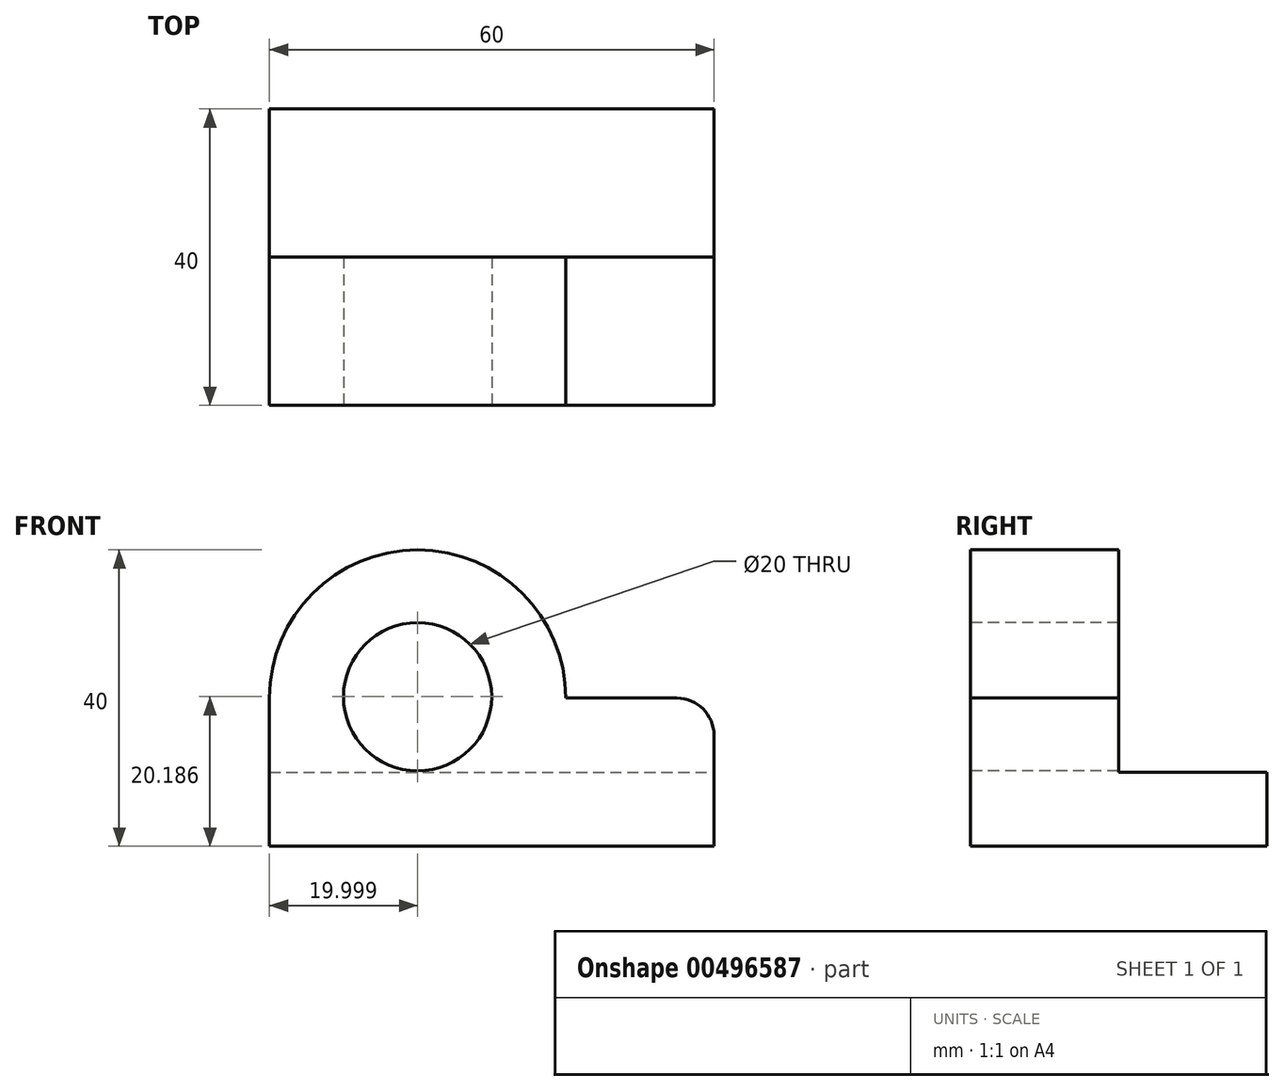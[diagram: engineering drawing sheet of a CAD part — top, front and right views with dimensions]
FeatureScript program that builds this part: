
annotation { "Feature Type Name" : "Feature", "Feature Type Description" : "" }
export const myFeature = defineFeature(function(context is Context, id is Id, definition is map)
    precondition{}
    {
        {
            var Q0;
            Q0=qCreatedBy(makeId("Top.planeOp"),FACE);
            var sketch = newSketch(context, id + "F0", { "sketchPlane" : qUnion([Q0])});
            skLineSegment(sketch, "E0.bottom", {"start": v(0, 0) * mm, "end": v(60, 0) * mm});
            skLineSegment(sketch, "E0.top", {"start": v(0, 40) * mm, "end": v(60, 40) * mm});
            skLineSegment(sketch, "E0.left", {"start": v(0, 0) * mm, "end": v(0, 40) * mm});
            skLineSegment(sketch, "E0.right", {"start": v(60, 0) * mm, "end": v(60, 40) * mm});
            skSolve(sketch);
        }
        {
            var Q0;
            Q0 = qSketchRegion(id + "F0", true);
            extrude(context, id + "F1", {"entities" : qUnion([Q0]), "depth" : 10 * mm});
        }
        {
            var Q0;
            Q0=makeQuery(id+"F1.opExtrude","SWEPT_FACE",FACE,{"disambiguationData":[OSD([sQuery(id+"F0.wireOp",EDGE,"E0.bottom")])]});
            var sketch = newSketch(context, id + "F2", { "sketchPlane" : qUnion([Q0])});
            skPoint(sketch, "E1", {"position": v(20, 20) * mm});
            skArc(sketch, "E2", {"start": v(40, 20) * mm, "mid": v(20, 40) * mm, "end": v(0, 20) * mm});
            skLineSegment(sketch, "E3", {"start": v(0, 20) * mm, "end": v(0, 10) * mm});
            skLineSegment(sketch, "E4", {"start": v(40, 20) * mm, "end": v(55, 20) * mm});
            skLineSegment(sketch, "E5", {"start": v(60, 15) * mm, "end": v(60, 10) * mm});
            skPoint(sketch, "E6.visualSharp", {"position": v(59.99, 20) * mm});
            skArc(sketch, "E6.filletArc", {"start": v(60, 15) * mm, "mid": v(58.53, 18.54) * mm, "end": v(55, 20) * mm});
            skLineSegment(sketch, "E7", {"start": v(0, 10) * mm, "end": v(60, 10) * mm});
            skSolve(sketch);
        }
        {
            var Q0;
            Q0 = qSketchRegion(id + "F2", true);
            extrude(context, id + "F3", {"entities" : qUnion([Q0]), "operationType" : NewBodyOperationType.ADD, "oppositeDirection" : true, "depth" : 20 * mm});
        }
        {
            var Q0;
            Q0=qCreatedBy(makeId("Front.planeOp"),FACE);
            var sketch = newSketch(context, id + "F4", { "sketchPlane" : qUnion([Q0])});
            skPoint(sketch, "E8", {"position": v(20, 20.19) * mm});
            skCircle(sketch, "E9", {"center": v(20, 20.19) * mm, "radius": 10 * mm});
            skSolve(sketch);
        }
        {
            var Q0;
            Q0 = qSketchRegion(id + "F4", true);
            extrude(context, id + "F5", {"entities" : qUnion([Q0]), "operationType" : NewBodyOperationType.REMOVE, "oppositeDirection" : true, "depth" : 25 * mm});
        }
    });
